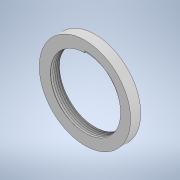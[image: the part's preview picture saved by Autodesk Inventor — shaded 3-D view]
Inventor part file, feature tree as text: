
AUTODESK INVENTOR PART (.ipt)
format: ipt  version: 2022.2 (Build 262287030, 287C)  size: 320,000 bytes
history: native  units: in
note: dims shown in document units (in); Inventor stores cm internally (conversion verified against a paired STEP export)
features: sketch x2, extrude x1, helix x1
ambient origin geometry x8: Origin, YZ Plane, XZ Plane, XY Plane, X Axis, Y Axis, Z Axis, Center Point
bodies: Solid1 (feature_tree)
feature tree (4):
  extrude  "Extrusion1"  Depth=0.1969in
  helix  "Coil1"  [1 undecoded]
  sketch  "Sketch1"  dims[d0=1.3437in d1=1.7717in d2=0.1969in d3=0.0in]
  sketch  "Sketch2"  dims[d4=0.0401in d5=0.0394in d6=0.6719in d7=0.0039in d8=0.0in d9=0.0394in d10=0.3937in d11=3.1496in d12=0.0in d13=90.0deg d14=90.0deg d15=0.0in d16=0.0in]
note: 1 required parameter value undecoded (feature->parameter linkage not recoverable at this tier; creation-order binding heuristic only, values carry confidence <= 0.55)
